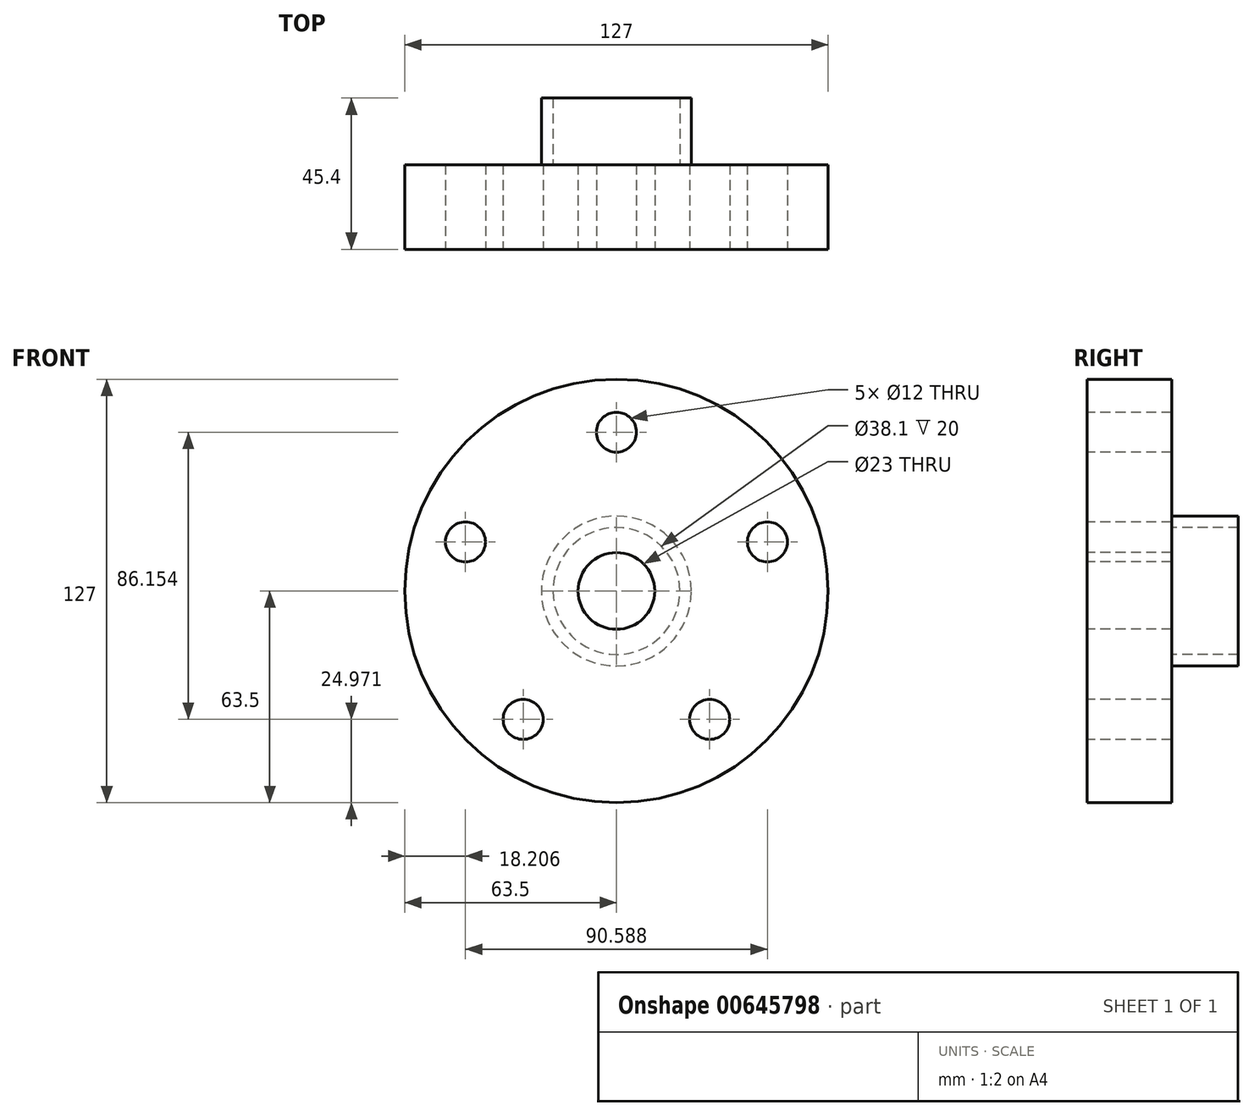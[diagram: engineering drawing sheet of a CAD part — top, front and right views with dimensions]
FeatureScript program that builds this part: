
annotation { "Feature Type Name" : "Feature", "Feature Type Description" : "" }
export const myFeature = defineFeature(function(context is Context, id is Id, definition is map)
    precondition{}
    {
        {
            var Q0;
            Q0=qCreatedBy(makeId("Front.planeOp"),FACE);
            var sketch = newSketch(context, id + "F0", { "sketchPlane" : qUnion([Q0])});
            skCircle(sketch, "E0", {"center": v(0, 0) * mm, "radius": 63.5 * mm});
            skSolve(sketch);
        }
        {
            var Q0;
            Q0=qSketchRegion(id+"F0",true);
            extrude(context, id + "F1", {"entities" : qUnion([Q0]), "depth" : 25.4 * mm});
        }
        {
            var Q0;
            Q0=makeQuery(id+"F1.opExtrude","CAP_FACE",FACE,{"disambiguationData":[OSD([sQuery(id+"F0.wireOp",EDGE,"E0")])],"isStart":true});
            var sketch = newSketch(context, id + "F2", { "sketchPlane" : qUnion([Q0])});
            skCircle(sketch, "E1", {"center": v(0, 0) * mm, "radius": 22.5 * mm});
            skCircle(sketch, "E2", {"center": v(0, 0) * mm, "radius": 19.05 * mm});
            skSolve(sketch);
        }
        {
            var Q0;
            Q0=qSketchRegion(id+"F2",true);
            extrude(context, id + "F3", {"entities" : qUnion([Q0]), "operationType" : NewBodyOperationType.ADD, "depth" : 20 * mm});
        }
        {
            var Q0;
            Q0=makeQuery(id+"F1.opExtrude","CAP_FACE",FACE,{"disambiguationData":[OSD([sQuery(id+"F0.wireOp",EDGE,"E0")])],"isStart":false});
            var sketch = newSketch(context, id + "F4", { "sketchPlane" : qUnion([Q0])});
            skCircle(sketch, "E3", {"center": v(0, 0) * mm, "radius": 11.5 * mm});
            skSolve(sketch);
        }
        {
            var Q0;
            Q0=qSketchRegion(id+"F4",true);
            extrude(context, id + "F5", {"entities" : qUnion([Q0]), "operationType" : NewBodyOperationType.REMOVE, "endBound" : BoundingType.UP_TO_NEXT, "oppositeDirection" : true, "depth" : 25.4 * mm});
        }
        {
            var Q0;
            Q0=makeQuery(id+"F1.opExtrude","CAP_FACE",FACE,{"disambiguationData":[OSD([sQuery(id+"F0.wireOp",EDGE,"E0")])],"isStart":false});
            var sketch = newSketch(context, id + "F6", { "sketchPlane" : qUnion([Q0])});
            skCircle(sketch, "E4", {"center": v(0, 0) * mm, "radius": 47.63 * mm, "construction": true});
            skCircle(sketch, "E5", {"center": v(0, 47.63) * mm, "radius": 6 * mm});
            skCircle(sketch, "E6.1.0", {"center": v(-45.3, 14.72) * mm, "radius": 6 * mm});
            skCircle(sketch, "E6.2.0", {"center": v(-28, -38.53) * mm, "radius": 6 * mm});
            skCircle(sketch, "E6.3.0", {"center": v(28, -38.53) * mm, "radius": 6 * mm});
            skCircle(sketch, "E6.4.0", {"center": v(45.3, 14.72) * mm, "radius": 6 * mm});
            skSolve(sketch);
        }
        {
            var Q0;
            Q0=qSketchRegion(id+"F6",true);
            extrude(context, id + "F7", {"entities" : qUnion([Q0]), "operationType" : NewBodyOperationType.REMOVE, "endBound" : BoundingType.UP_TO_NEXT, "oppositeDirection" : true, "depth" : 25 * mm});
        }
    });
